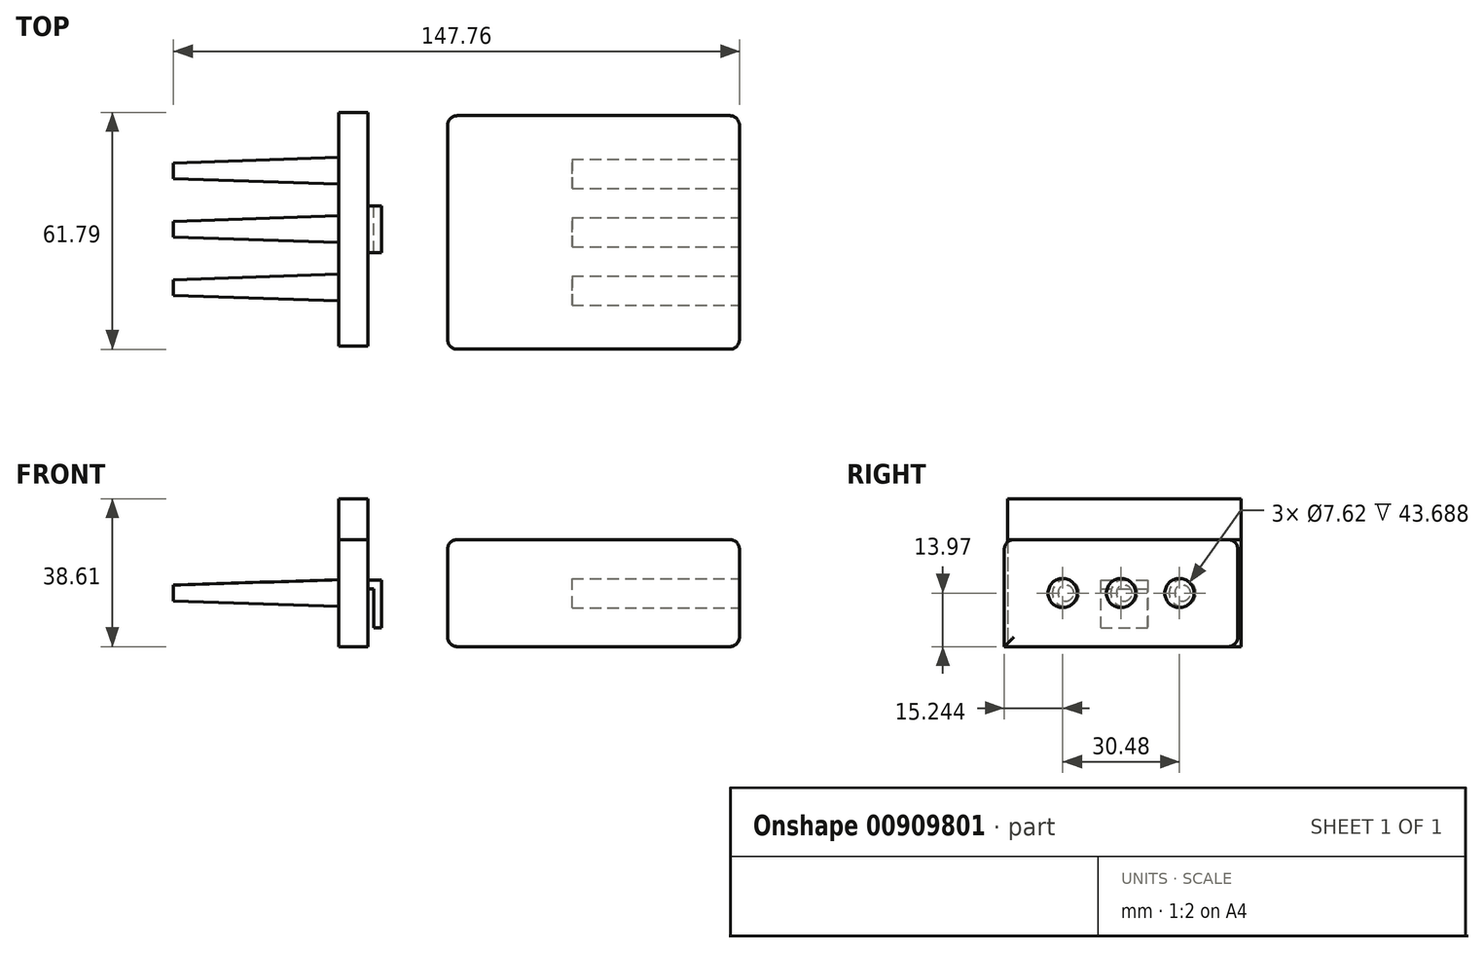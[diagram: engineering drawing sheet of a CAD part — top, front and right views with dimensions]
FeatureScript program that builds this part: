
annotation { "Feature Type Name" : "Feature", "Feature Type Description" : "" }
export const myFeature = defineFeature(function(context is Context, id is Id, definition is map)
    precondition{}
    {
        {
            var Q0;
            Q0=qCreatedBy(makeId("Top.planeOp"),FACE);
            var sketch = newSketch(context, id + "F0", { "sketchPlane" : qUnion([Q0])});
            skPoint(sketch, "E0.middle", {"position": v(0, 0) * mm});
            skLineSegment(sketch, "E1.bottom", {"start": v(24.57, 29.65) * mm, "end": v(100.77, 29.65) * mm});
            skLineSegment(sketch, "E1.top", {"start": v(24.57, -31.3) * mm, "end": v(100.77, -31.3) * mm});
            skLineSegment(sketch, "E1.left", {"start": v(24.57, 29.65) * mm, "end": v(24.57, -31.3) * mm});
            skLineSegment(sketch, "E1.right", {"start": v(100.77, 29.65) * mm, "end": v(100.77, -31.3) * mm});
            skLineSegment(sketch, "E2.bottom", {"start": v(3.8, -30.48) * mm, "end": v(-3.81, -30.48) * mm});
            skLineSegment(sketch, "E2.top", {"start": v(3.81, 30.48) * mm, "end": v(-3.8, 30.48) * mm});
            skLineSegment(sketch, "E2.left", {"start": v(3.8, -30.48) * mm, "end": v(3.81, 30.48) * mm});
            skLineSegment(sketch, "E2.right", {"start": v(-3.81, -30.48) * mm, "end": v(-3.8, 30.48) * mm});
            skSolve(sketch);
        }
        {
            var Q0;
            Q0=makeQuery(id+"F0.imprint","IMPRINT",FACE,{"disambiguationData":[TD([[makeQuery(id+"F0.imprint","IMPRINT",EDGE,{"derivedFrom":sQuery(id+"F0.wireOp",EDGE,"E2.bottom")}),-1.0]])]});
            var Q1;
            Q1=makeQuery(id+"F0.imprint","IMPRINT",FACE,{"disambiguationData":[TD([[makeQuery(id+"F0.imprint","IMPRINT",EDGE,{"derivedFrom":sQuery(id+"F0.wireOp",EDGE,"E1.bottom")}),-1.0]])]});
            extrude(context, id + "F1", {"entities" : qUnion([Q0, Q1]), "depth" : 27.94 * mm, "offsetDistance" : 25.4 * mm});
        }
        {
            var Q0;
            Q0=makeQuery(id+"F1.opExtrude","CAP_FACE",FACE,{"disambiguationData":[OSD([sQuery(id+"F0.wireOp",EDGE,"E2.bottom"),sQuery(id+"F0.wireOp",EDGE,"E2.top"),sQuery(id+"F0.wireOp",EDGE,"E2.left"),sQuery(id+"F0.wireOp",EDGE,"E2.right")])],"isStart":false});
            extrude(context, id + "F2", {"entities" : qUnion([Q0]), "depth" : 10.67 * mm, "offsetDistance" : 25.4 * mm});
        }
        {
            var Q0;
            Q0=makeQuery(id+"F1.opExtrude","SWEPT_FACE",FACE,{"disambiguationData":[OSD([sQuery(id+"F0.wireOp",EDGE,"E1.right")])]});
            var sketch = newSketch(context, id + "F3", { "sketchPlane" : qUnion([Q0])});
            skLineSegment(sketch, "E3", {"start": v(-31.3, 13.97) * mm, "end": v(-16.07, 13.97) * mm});
            skLineSegment(sketch, "E4", {"start": v(-16.07, 13.97) * mm, "end": v(-0.83, 13.97) * mm});
            skLineSegment(sketch, "E5", {"start": v(-0.83, 13.97) * mm, "end": v(14.41, 13.97) * mm});
            skLineSegment(sketch, "E6", {"start": v(14.41, 13.97) * mm, "end": v(29.65, 13.97) * mm});
            skCircle(sketch, "E7", {"center": v(-16.07, 13.97) * mm, "radius": 3.81 * mm});
            skCircle(sketch, "E8", {"center": v(-0.83, 13.97) * mm, "radius": 3.81 * mm});
            skCircle(sketch, "E9", {"center": v(14.41, 13.97) * mm, "radius": 3.81 * mm});
            skSolve(sketch);
        }
        {
            var Q0;
            {var subQ0=sQuery(id+"F3.wireOp",EDGE,"E4");var subQ1=sQuery(id+"F3.wireOp",EDGE,"E3");var subQ2=makeQuery(id+"F3.imprint","INTERSECT",VERTEX,{"derivedFrom":[subQ1,subQ0]});Q0=makeQuery(id+"F3.imprint","IMPRINT",FACE,{"disambiguationData":[TD([[makeQuery(id+"F3.imprint","IMPRINT",EDGE,{"disambiguationData":[TD([[subQ2,1.0]])],"derivedFrom":subQ1}),-1.0]])]});}
            var Q1;
            {var subQ0=sQuery(id+"F3.wireOp",EDGE,"E4");var subQ1=sQuery(id+"F3.wireOp",EDGE,"E3");var subQ2=makeQuery(id+"F3.imprint","INTERSECT",VERTEX,{"derivedFrom":[subQ1,subQ0]});Q1=makeQuery(id+"F3.imprint","IMPRINT",FACE,{"disambiguationData":[TD([[makeQuery(id+"F3.imprint","IMPRINT",EDGE,{"disambiguationData":[TD([[subQ2,1.0]])],"derivedFrom":subQ1}),1.0]])]});}
            var Q2;
            {var subQ0=sQuery(id+"F3.wireOp",EDGE,"E5");var subQ1=sQuery(id+"F3.wireOp",EDGE,"E4");var subQ2=makeQuery(id+"F3.imprint","INTERSECT",VERTEX,{"derivedFrom":[subQ1,subQ0]});Q2=makeQuery(id+"F3.imprint","IMPRINT",FACE,{"disambiguationData":[TD([[makeQuery(id+"F3.imprint","IMPRINT",EDGE,{"disambiguationData":[TD([[subQ2,1.0]])],"derivedFrom":subQ1}),-1.0]])]});}
            var Q3;
            {var subQ0=sQuery(id+"F3.wireOp",EDGE,"E5");var subQ1=sQuery(id+"F3.wireOp",EDGE,"E4");var subQ2=makeQuery(id+"F3.imprint","INTERSECT",VERTEX,{"derivedFrom":[subQ1,subQ0]});Q3=makeQuery(id+"F3.imprint","IMPRINT",FACE,{"disambiguationData":[TD([[makeQuery(id+"F3.imprint","IMPRINT",EDGE,{"disambiguationData":[TD([[subQ2,1.0]])],"derivedFrom":subQ1}),1.0]])]});}
            var Q4;
            {var subQ0=sQuery(id+"F3.wireOp",EDGE,"E6");var subQ1=sQuery(id+"F3.wireOp",EDGE,"E5");var subQ2=makeQuery(id+"F3.imprint","INTERSECT",VERTEX,{"derivedFrom":[subQ1,subQ0]});Q4=makeQuery(id+"F3.imprint","IMPRINT",FACE,{"disambiguationData":[TD([[makeQuery(id+"F3.imprint","IMPRINT",EDGE,{"disambiguationData":[TD([[subQ2,1.0]])],"derivedFrom":subQ1}),-1.0]])]});}
            var Q5;
            {var subQ0=sQuery(id+"F3.wireOp",EDGE,"E6");var subQ1=sQuery(id+"F3.wireOp",EDGE,"E5");var subQ2=makeQuery(id+"F3.imprint","INTERSECT",VERTEX,{"derivedFrom":[subQ1,subQ0]});Q5=makeQuery(id+"F3.imprint","IMPRINT",FACE,{"disambiguationData":[TD([[makeQuery(id+"F3.imprint","IMPRINT",EDGE,{"disambiguationData":[TD([[subQ2,1.0]])],"derivedFrom":subQ1}),1.0]])]});}
            var Q6;
            Q6=sQuery(id+"F3.wireOp",EDGE,"E7");
            var Q7;
            Q7=sQuery(id+"F3.wireOp",EDGE,"E8");
            var Q8;
            Q8=sQuery(id+"F3.wireOp",EDGE,"E9");
            extrude(context, id + "F4", {"entities" : qUnion([Q0, Q1, Q2, Q3, Q4, Q5]), "operationType" : NewBodyOperationType.REMOVE, "surfaceEntities" : qUnion([Q6, Q7, Q8]), "oppositeDirection" : true, "depth" : 43.69 * mm, "offsetDistance" : 25.4 * mm});
        }
        {
            var Q0;
            Q0=makeQuery(id+"F1.opExtrude","SWEPT_FACE",FACE,{"disambiguationData":[OSD([sQuery(id+"F0.wireOp",EDGE,"E2.right")])]});
            var sketch = newSketch(context, id + "F5", { "sketchPlane" : qUnion([Q0])});
            skLineSegment(sketch, "E10", {"start": v(-30.48, 0) * mm, "end": v(-30.48, 13.97) * mm});
            skLineSegment(sketch, "E11", {"start": v(-30.48, 13.97) * mm, "end": v(-15.24, 13.97) * mm});
            skLineSegment(sketch, "E12", {"start": v(-15.24, 13.97) * mm, "end": v(0, 13.97) * mm});
            skLineSegment(sketch, "E13", {"start": v(0, 13.97) * mm, "end": v(15.24, 13.97) * mm});
            skLineSegment(sketch, "E14", {"start": v(15.24, 13.97) * mm, "end": v(30.48, 13.97) * mm});
            skCircle(sketch, "E15", {"center": v(-15.24, 13.97) * mm, "radius": 3.5 * mm});
            skCircle(sketch, "E16", {"center": v(0, 13.97) * mm, "radius": 3.5 * mm});
            skCircle(sketch, "E17", {"center": v(15.24, 13.97) * mm, "radius": 3.5 * mm});
            skSolve(sketch);
        }
        {
            var Q0;
            Q0 = qSketchRegion(id + "F5", true);
            extrude(context, id + "F6", {"entities" : qUnion([Q0]), "operationType" : NewBodyOperationType.ADD, "depth" : 43.18 * mm, "offsetDistance" : 25.4 * mm, "hasDraft" : true, "draftAngle" : 1.89 * degree, "draftPullDirection" : true});
        }
        {
            var Q0;
            Q0=makeQuery(id+"F1.opExtrude","CAP_EDGE",EDGE,{"disambiguationData":[OSD([sQuery(id+"F0.wireOp",EDGE,"E1.top")])],"isStart":false});
            var Q1;
            Q1=makeQuery(id+"F1.opExtrude","SWEPT_EDGE",EDGE,{"disambiguationData":[OSD([sQuery(id+"F0.wireOp",EDGE,"E1.top"),sQuery(id+"F0.wireOp",EDGE,"E1.right")])]});
            var Q2;
            Q2=makeQuery(id+"F1.opExtrude","CAP_EDGE",EDGE,{"disambiguationData":[OSD([sQuery(id+"F0.wireOp",EDGE,"E1.right")])],"isStart":false});
            var Q3;
            Q3=makeQuery(id+"F1.opExtrude","CAP_EDGE",EDGE,{"disambiguationData":[OSD([sQuery(id+"F0.wireOp",EDGE,"E1.right")])],"isStart":true});
            var Q4;
            Q4=makeQuery(id+"F1.opExtrude","SWEPT_FACE",FACE,{"disambiguationData":[OSD([sQuery(id+"F0.wireOp",EDGE,"E1.bottom")])]});
            var Q5;
            Q5=makeQuery(id+"F1.opExtrude","SWEPT_FACE",FACE,{"disambiguationData":[OSD([sQuery(id+"F0.wireOp",EDGE,"E1.left")])]});
            fillet(context, id + "F7", {"entities" : qUnion([Q0, Q1, Q2, Q3, Q4, Q5]), "radius" : 2.54 * mm, "tangentPropagation" : true, "allowEdgeOverflow" : false});
        }
        {
            var Q0;
            Q0=makeQuery(id+"F1.opExtrude","SWEPT_FACE",FACE,{"disambiguationData":[OSD([sQuery(id+"F0.wireOp",EDGE,"E2.left")])]});
            var sketch = newSketch(context, id + "F8", { "sketchPlane" : qUnion([Q0])});
            skLineSegment(sketch, "E18", {"start": v(-30.48, 0) * mm, "end": v(-30.48, 7.52) * mm});
            skLineSegment(sketch, "E19", {"start": v(-30.48, 7.52) * mm, "end": v(-18.29, 7.52) * mm});
            skLineSegment(sketch, "E20", {"start": v(-18.29, 7.52) * mm, "end": v(-6.1, 7.52) * mm});
            skLineSegment(sketch, "E21", {"start": v(-6.1, 7.52) * mm, "end": v(6.1, 7.52) * mm});
            skLineSegment(sketch, "E22", {"start": v(6.1, 7.52) * mm, "end": v(18.29, 7.52) * mm});
            skLineSegment(sketch, "E23", {"start": v(18.29, 7.52) * mm, "end": v(30.48, 7.52) * mm});
            skLineSegment(sketch, "E24", {"start": v(-6.1, 7.52) * mm, "end": v(-6.1, 15.04) * mm});
            skLineSegment(sketch, "E25", {"start": v(-6.1, 15.04) * mm, "end": v(-6.1, 17.32) * mm});
            skLineSegment(sketch, "E26", {"start": v(-6.1, 17.32) * mm, "end": v(6.1, 17.32) * mm});
            skLineSegment(sketch, "E27", {"start": v(6.1, 17.32) * mm, "end": v(6.1, 7.52) * mm});
            skLineSegment(sketch, "E28", {"start": v(-6.1, 15.04) * mm, "end": v(6.1, 15.04) * mm});
            skSolve(sketch);
        }
        {
            var Q0;
            Q0=makeQuery(id+"F8.imprint","IMPRINT",FACE,{"disambiguationData":[TD([[makeQuery(id+"F8.imprint","IMPRINT",EDGE,{"derivedFrom":sQuery(id+"F8.wireOp",EDGE,"E25")}),-1.0]])]});
            extrude(context, id + "F9", {"entities" : qUnion([Q0]), "operationType" : NewBodyOperationType.ADD, "depth" : 3.5 * mm, "offsetDistance" : 25.4 * mm});
        }
        {
            var Q0;
            Q0=makeQuery(id+"F9.opExtrude","SWEPT_FACE",FACE,{"disambiguationData":[OSD([sQuery(id+"F8.wireOp",EDGE,"E28")])]});
            var sketch = newSketch(context, id + "F10", { "sketchPlane" : qUnion([Q0])});
            skLineSegment(sketch, "E29", {"start": v(3.8, 6.1) * mm, "end": v(5.33, 6.1) * mm});
            skLineSegment(sketch, "E30", {"start": v(5.33, 6.1) * mm, "end": v(5.33, -6.1) * mm});
            skPoint(sketch, "E30.endSnap0", {"position": v(5.56, -6.1) * mm});
            skLineSegment(sketch, "E31", {"start": v(5.33, 6.1) * mm, "end": v(7.32, 6.1) * mm});
            skSolve(sketch);
        }
        {
            var Q0;
            {var subQ0=sQuery(id+"F10.wireOp",EDGE,"E30");Q0=makeQuery(id+"F10.imprint","IMPRINT",FACE,{"disambiguationData":[TD([[makeQuery(id+"F10.imprint","IMPRINT",EDGE,{"derivedFrom":subQ0}),1.0]])]});}
            extrude(context, id + "F11", {"entities" : qUnion([Q0]), "operationType" : NewBodyOperationType.ADD, "depth" : 10.16 * mm, "offsetDistance" : 25.4 * mm});
        }
    });
